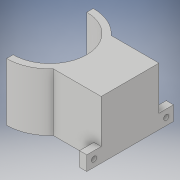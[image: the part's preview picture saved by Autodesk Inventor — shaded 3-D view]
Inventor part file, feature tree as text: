
AUTODESK INVENTOR PART (.ipt)
format: ipt  version: 2019 (Build 230136000, 136)  size: 180,736 bytes
history: native  units: in
note: dims shown in document units (in); Inventor stores cm internally (conversion verified against a paired STEP export)
features: extrude x5, sketch x5, thicken_offset x1
ambient origin geometry x8: Origin, YZ Plane, XZ Plane, XY Plane, X Axis, Y Axis, Z Axis, Center Point
bodies: Solid1 (feature_tree)
feature tree (11):
  extrude  "Extrusion1"  Depth=3.0in
  extrude  "Extrusion2"  Depth=1.5in
  extrude  "Extrusion3"  Depth=1.0in
  extrude  "Extrusion4"  Depth=0.25in
  extrude  "Extrusion5"  Depth=0.25in
  thicken_offset  "Thicken1"
  sketch  "Sketch1"  dims[d0=2.55in d1=3.0in]
  sketch  "Sketch2"  dims[d2=3.0in d3=0.0in d4=1.5in]
  sketch  "Sketch3"  dims[d5=1.0in d6=1.0in]
  sketch  "Sketch4"  dims[d7=3.0in d8=0.0in d9=0.25in]
  sketch  "Sketch5"  dims[d10=0.5in d11=0.25in d12=0.5in d13=3.0in d14=0.0in d15=0.5in d16=0.5in d17=0.5in d18=0.5in d19=0.5in d20=0.5in d21=0.5in d22=0.5in d23=1.4375in d24=0.0in d25=0.1772in d26=0.1772in d27=0.1772in d28=0.1772in d29=1.4375in d30=0.0in d31=1.0in d32=1.0in]
